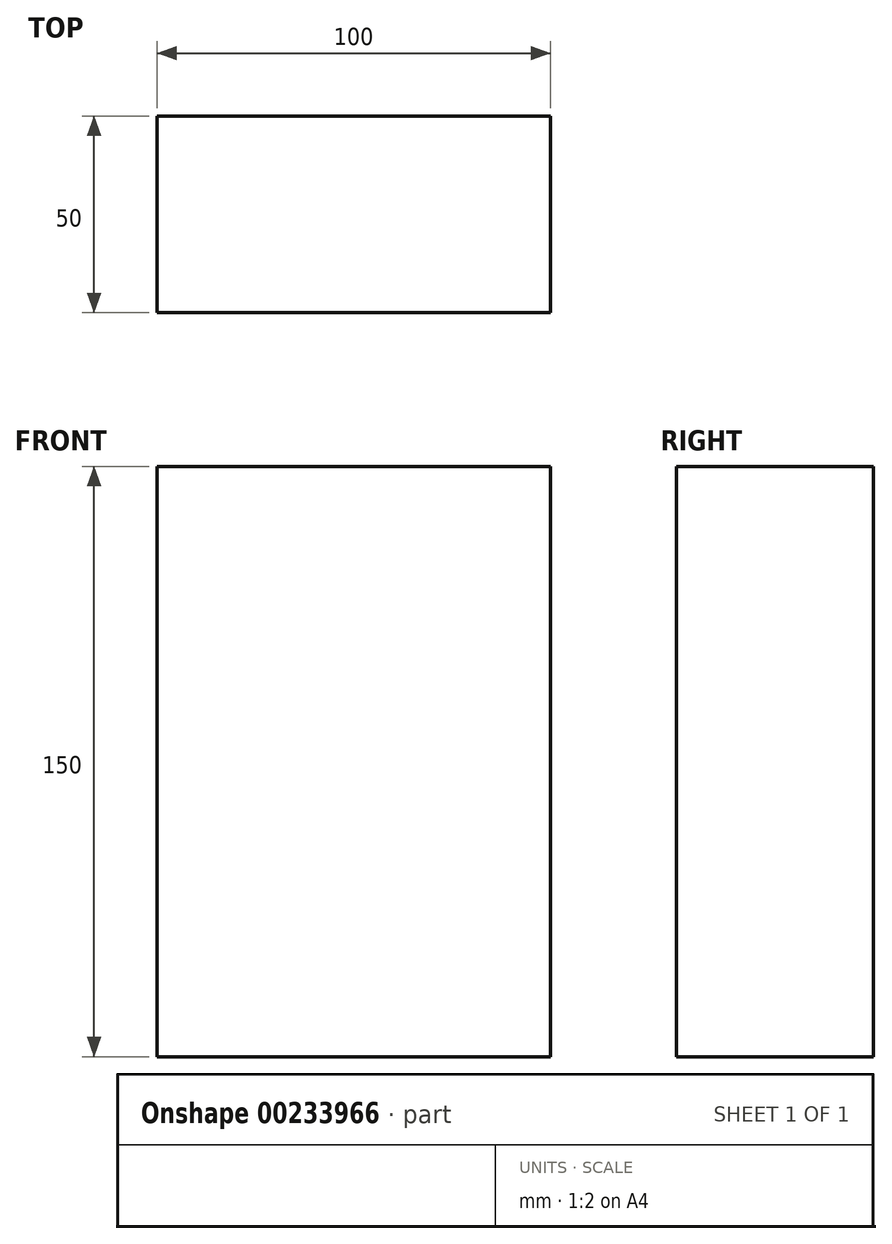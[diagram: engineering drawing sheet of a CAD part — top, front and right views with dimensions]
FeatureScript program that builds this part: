
annotation { "Feature Type Name" : "Feature", "Feature Type Description" : "" }
export const myFeature = defineFeature(function(context is Context, id is Id, definition is map)
    precondition{}
    {
        {
            var Q0;
            Q0=qCreatedBy(makeId("Top.planeOp"),FACE);
            var sketch = newSketch(context, id + "F0", { "sketchPlane" : qUnion([Q0])});
            skLineSegment(sketch, "E0.bottom", {"start": v(50, -25) * mm, "end": v(-50, -25) * mm});
            skLineSegment(sketch, "E0.top", {"start": v(50, 25) * mm, "end": v(-50, 25) * mm});
            skLineSegment(sketch, "E0.left", {"start": v(50, -25) * mm, "end": v(50, 25) * mm});
            skLineSegment(sketch, "E0.right", {"start": v(-50, -25) * mm, "end": v(-50, 25) * mm});
            skPoint(sketch, "E0.middle", {"position": v(0, 0) * mm});
            skSolve(sketch);
        }
        {
            var Q0;
            Q0=makeQuery(id+"F0.imprint","IMPRINT",FACE,{"disambiguationData":[TD([[makeQuery(id+"F0.imprint","IMPRINT",EDGE,{"derivedFrom":sQuery(id+"F0.wireOp",EDGE,"E0.bottom")}),-1.0]])]});
            extrude(context, id + "F1", {"entities" : qUnion([Q0]), "depth" : 150 * mm});
        }
    });
